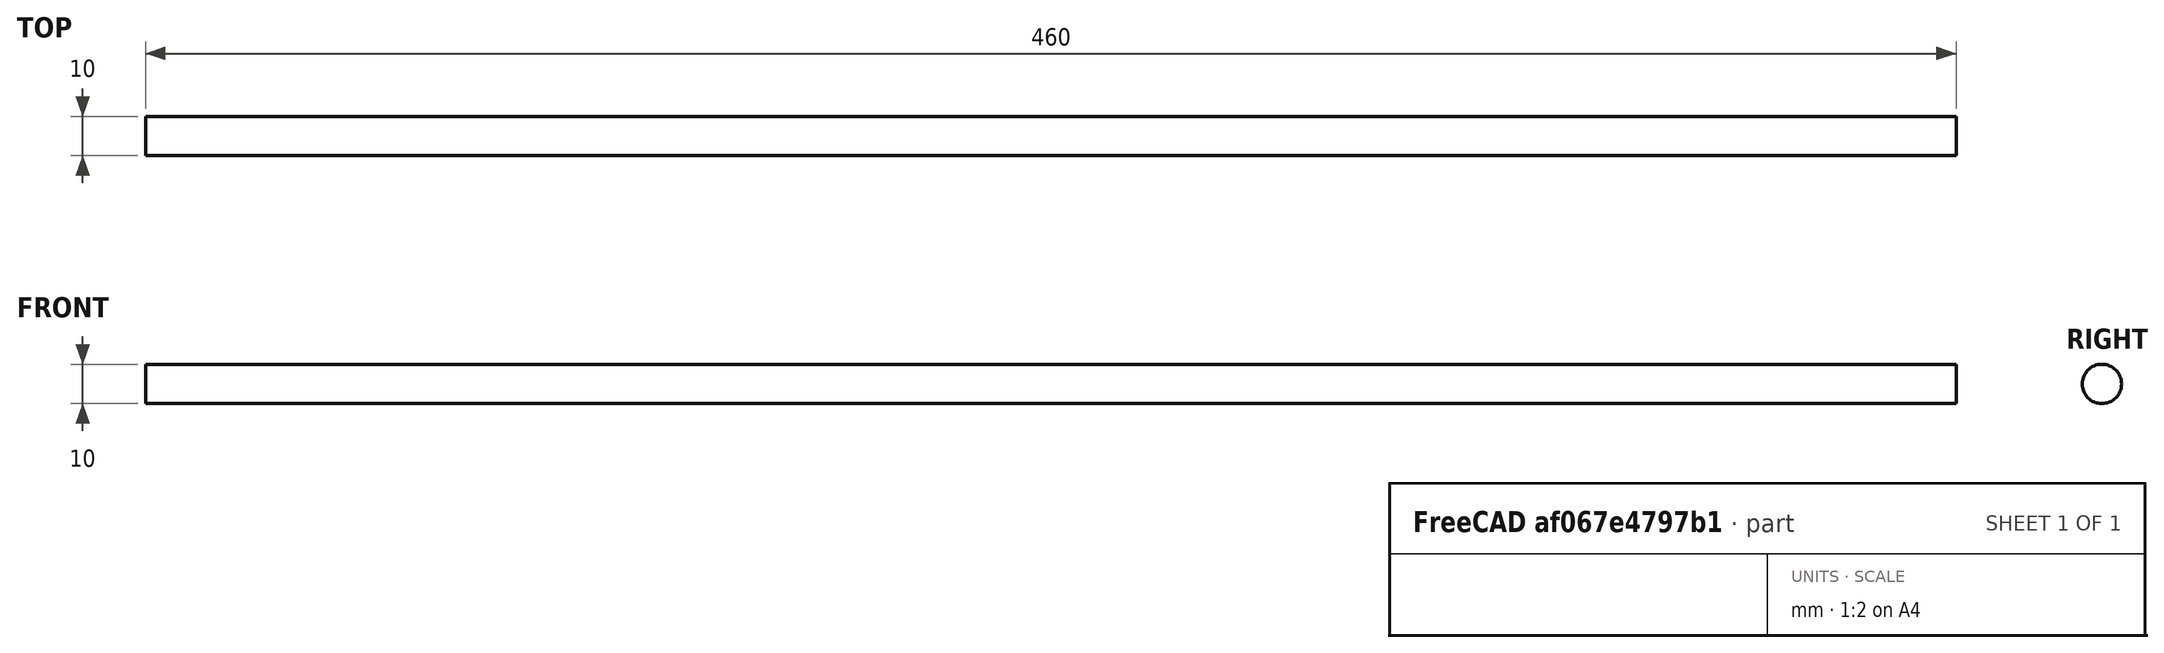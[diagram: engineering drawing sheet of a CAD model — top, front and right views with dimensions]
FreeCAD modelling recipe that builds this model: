
FCSTD DOCUMENT  (FreeCAD 0.21R33771 (Git))
Label: x axis rod
License: All rights reserved
LicenseURL: http://en.wikipedia.org/wiki/All_rights_reserved
objects: Sketcher::SketchObject×1, PartDesign::Pad×1, PartDesign::Body×1
note: 4 computed .brp shape members not serialized (recipe doc carries the construction recipe); baked Part::Feature solids carry a one-line shape summary decoded from their .brp

FEATURE [Sketcher::SketchObject] Sketch
  FullyConstrained = true
  MapMode = 5
  Placement = pos=(0,0,0) rot=(0.57735,0.57735,0.57735;2.0944rad)
  Support = -> [YZ_Plane]
  sketch-geometry (1):
    g0: Circle CenterX=0 CenterY=0 CenterZ=0 NormalX=0 NormalY=0 NormalZ=1 AngleXU=0 Radius=5
  constraints (2):
    c: Coincident(g0,g-1)
    c: Radius(g0) = 5
FEATURE [PartDesign::Pad] Pad
  Direction = (1,-2e-16,3e-16)
  Length = 460
  Length2 = 10
  Placement = pos=(0,0,0) rot=(1,1,1;2.0944rad)
  Profile = -> Sketch
  ReferenceAxis = -> Sketch [N_Axis]
  Type = 0
FEATURE [PartDesign::Body] Body
  Group = -> [Sketch,Pad]
  Origin = -> Origin
  Tip = -> Pad
